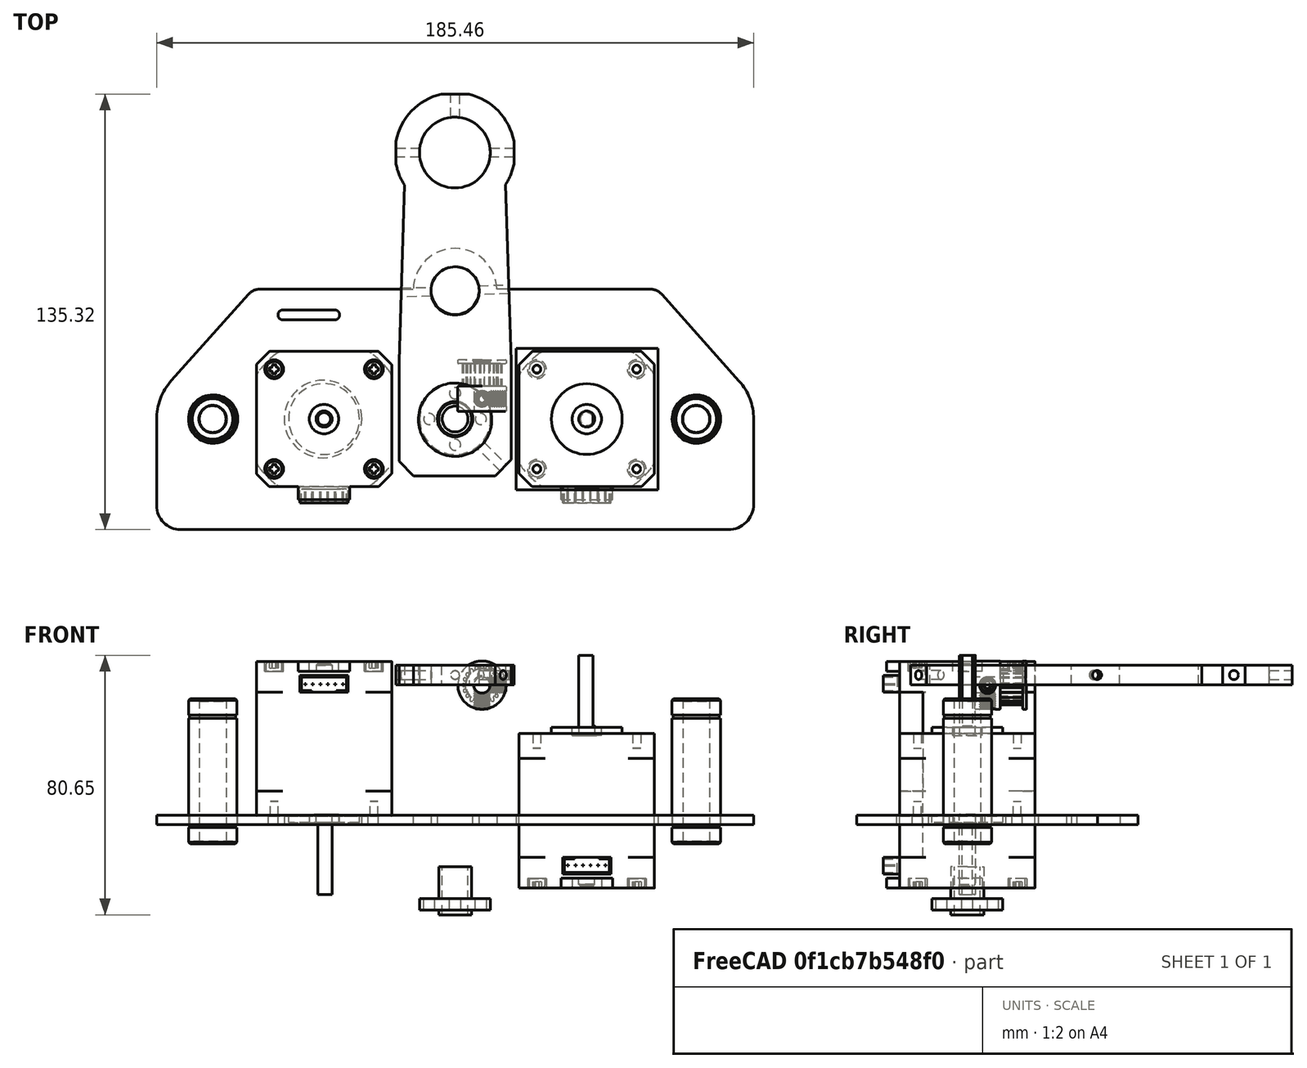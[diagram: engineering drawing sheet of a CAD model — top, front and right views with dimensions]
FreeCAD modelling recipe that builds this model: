
FCSTD DOCUMENT  (FreeCAD 1.0R38641 +468 (Git))
Label: ZAXIS-ASSY
License: All rights reserved
LicenseURL: https://en.wikipedia.org/wiki/All_rights_reserved
objects: Part::Feature×8, Sketcher::SketchObject×6, PartDesign::Pocket×4, PartDesign::Body×4, Mesh::Feature×2, App::Part×2, PartDesign::Pad×2, PartDesign::FeatureBase×2
note: 46 computed .brp shape members not serialized (recipe doc carries the construction recipe); baked Part::Feature solids carry a one-line shape summary decoded from their .brp

FEATURE [Mesh::Feature] Arm_Base_ZHub_Top_1_0_0  label="Arm_Base_ZHub_Top_1.0.0"
  Placement = pos=(-7.1,-2.4,28.8) rot=(0,0,1;3.14159rad)
FEATURE [Mesh::Feature] Arm_Base_MotorPlate_1_1_2  label="Arm_Base_MotorPlate_1.1.2"
  Placement = pos=(0,2.2,0) rot=(0,0,1;0rad)
FEATURE [App::Part] Part  label="ZAXIS"
  Group = -> [Arm_Base_ZHub_Top_1_0_0,Arm_Base_MotorPlate_1_1_2]
  Origin = -> Origin
FEATURE [Sketcher::SketchObject] Sketch002
  ArcFitTolerance = 1e-06
  AttachmentSupport = -> [XY_Plane003]
  FullyConstrained = false
  MakeInternals = false
  MapMode = 5
  sketch-geometry (22):
    g0: Circle CenterX=0 CenterY=0 CenterZ=0 NormalX=0 NormalY=0 NormalZ=1 AngleXU=0 Radius=7.5
    g1: LineSegment [constr] StartX=-29.959 StartY=-40 StartZ=0 EndX=43.5596 EndY=-40 EndZ=0
    g2: LineSegment [constr] StartX=-51.7591 StartY=43 StartZ=0 EndX=60.4533 EndY=43 EndZ=0
    g3: Circle CenterX=0 CenterY=-40 CenterZ=0 NormalX=0 NormalY=0 NormalZ=1 AngleXU=0 Radius=11.4
    g4: Circle CenterX=0.0652184 CenterY=43 CenterZ=0 NormalX=0 NormalY=0 NormalZ=1 AngleXU=0 Radius=11
    g5: LineSegment StartX=17.4186 StartY=-21.7716 StartZ=0 EndX=15.72 EndY=32.896 EndZ=0
    g6: LineSegment StartX=-17.4186 StartY=-21.7716 StartZ=0 EndX=-15.72 EndY=33.0441 EndZ=0
    g7: LineSegment StartX=-4.33292 StartY=61.137 StartZ=0 EndX=4.33292 EndY=61.137 EndZ=0
    g8: LineSegment StartX=-18.2601 StartY=39.4677 StartZ=0 EndX=-18.2601 EndY=46.5323 EndZ=0
    g9: LineSegment StartX=18.3596 StartY=39.4677 StartZ=0 EndX=18.3596 EndY=46.5323 EndZ=0
    g10: ArcOfCircle CenterX=0.0652184 CenterY=43 CenterZ=0 NormalX=0 NormalY=0 NormalZ=1 AngleXU=0 Radius=18.6626 StartAngle=1.8087 EndAngle=2.95117
    g11: ArcOfCircle CenterX=0.0652184 CenterY=43 CenterZ=0 NormalX=0 NormalY=0 NormalZ=1 AngleXU=0 Radius=18.6323 StartAngle=0.190736 EndAngle=1.3397
    g12: ArcOfCircle CenterX=0.0652184 CenterY=43 CenterZ=0 NormalX=0 NormalY=0 NormalZ=1 AngleXU=0 Radius=18.6323 StartAngle=5.71003 EndAngle=6.09245
    g13: ArcOfCircle CenterX=0.0652184 CenterY=43 CenterZ=0 NormalX=0 NormalY=0 NormalZ=1 AngleXU=0 Radius=18.6626 StartAngle=3.33202 EndAngle=3.70429
    g14: LineSegment [constr] StartX=0 StartY=-40 StartZ=0 EndX=-21.718 EndY=-61.718 EndZ=0
    g15: LineSegment [constr] StartX=0 StartY=-40 StartZ=0 EndX=21.718 EndY=-61.718 EndZ=0
    g16: ArcOfCircle [constr] CenterX=0 CenterY=-40 CenterZ=0 NormalX=0 NormalY=0 NormalZ=1 AngleXU=0 Radius=30.7139 StartAngle=3.92699 EndAngle=5.49779
    g17: LineSegment StartX=-17.4186 StartY=-52.4548 StartZ=0 EndX=-12.4548 EndY=-57.4186 EndZ=0
    g18: LineSegment StartX=17.4186 StartY=-52.8964 StartZ=0 EndX=12.8964 EndY=-57.4186 EndZ=0
    g19: LineSegment StartX=-12.4548 StartY=-57.4186 StartZ=0 EndX=12.8964 EndY=-57.4186 EndZ=0
    g20: LineSegment StartX=17.4186 StartY=-52.8964 StartZ=0 EndX=17.4186 EndY=-21.7716 EndZ=0
    g21: LineSegment StartX=-17.4186 StartY=-52.4548 StartZ=0 EndX=-17.4186 EndY=-21.7716 EndZ=0
  constraints (46):
    c: Coincident(g0,g-1)
    c: Diameter(g0) = 15
    c: Horizontal(g1)
    c: Horizontal(g2)
    c: PointOnObject(g3,g1)
    c: Diameter(g3) = 22.8
    c: DistanceY(g1,g0) = 40
    c: DistanceY(g0,g2) = 43
    c: PointOnObject(g4,g2)
    c: Vertical(g9)
    c: Symmetric(g8,g8,g2)
    c: Equal(g9,g8)
    c: Coincident(g10,g4)
    c: Coincident(g10,g7)
    c: Coincident(g10,g8)
    c: Coincident(g11,g4)
    c: Coincident(g11,g7)
    c: Coincident(g11,g9)
    c: Coincident(g12,g4)
    c: Coincident(g12,g9)
    c: Coincident(g12,g5)
    c: Coincident(g13,g4)
    c: Coincident(g13,g8)
    c: Coincident(g13,g6)
    c: Diameter(g4) = 22
    c: Horizontal(g9,g8)
    c: PointOnObject(g3,g-2)
    c: Symmetric(g6,g5,g-2)
    c: Coincident(g14,g3)
    c: Coincident(g15,g3)
    c: Perpendicular(g15,g14)
    c: Angle(g15,g1) = 0.785398
    c: Coincident(g16,g3)
    c: Coincident(g16,g14)
    c: Coincident(g16,g15)
    c: Symmetric(g17,g17,g14)
    c: Symmetric(g18,g18,g15)
    c: Coincident(g19,g17)
    c: Coincident(g19,g18)
    c: Horizontal(g19)
    c: Symmetric(g7,g7,g-2)
    c: Coincident(g20,g18)
    c: Coincident(g21,g17)
    c: Coincident(g21,g6)
    c: Coincident(g20,g5)
    c: Parallel(g20,g21)
FEATURE [PartDesign::Pad] Pad002
  Direction = (0,0,1)
  Length = 6
  Length2 = 10
  Profile = -> Sketch002
  ReferenceAxis = -> Sketch002 [N_Axis]
  Refine = true
  Suppressed = false
  Type = 0
FEATURE [Sketcher::SketchObject] Sketch003
  ArcFitTolerance = 1e-06
  AttachmentSupport = -> [Pad002]
  ExternalGeometry = -> [Pad002]
  FullyConstrained = false
  MakeInternals = false
  MapMode = 5
  Placement = pos=(-34.9367,-34.9367,0) rot=(0.862856,-0.357407,-0.357407;1.71777rad)
  sketch-geometry (2):
    g0: Circle CenterX=28.2843 CenterY=3 CenterZ=0 NormalX=0 NormalY=0 NormalZ=1 AngleXU=0 Radius=1.4
    g1: LineSegment [constr] StartX=28.2843 StartY=3 StartZ=0 EndX=28.2843 EndY=10.6288 EndZ=0
  constraints (4):
    c: Diameter(g0) = 2.8
    c: DistanceY(g0,g-3) = 3
    c: Coincident(g1,g0)
    c: Symmetric(g-3,g-3,g1)
FEATURE [PartDesign::Pocket] Pocket
  BaseFeature = -> Pad002
  Direction = (0.707107,0.707107,0)
  Length = 20
  Length2 = 5
  Profile = -> Sketch003
  ReferenceAxis = -> Sketch003 [N_Axis]
  Refine = true
  Suppressed = false
  Type = 0
FEATURE [Sketcher::SketchObject] Sketch004
  ArcFitTolerance = 1e-06
  AttachmentSupport = -> [Pocket]
  FullyConstrained = true
  MakeInternals = false
  MapMode = 5
  Placement = pos=(-16.7279,0.51835,0) rot=(-0.565428,0.58322,0.58322;4.17081rad)
  sketch-geometry (1):
    g0: Circle CenterX=0 CenterY=3 CenterZ=0 NormalX=0 NormalY=0 NormalZ=1 AngleXU=0 Radius=1.4
  constraints (3):
    c: PointOnObject(g0,g-2)
    c: DistanceY(g-1,g0) = 3
    c: Diameter(g0) = 2.8
FEATURE [PartDesign::Pocket] Pocket001
  BaseFeature = -> Pocket
  Direction = (0.99952,-0.0309723,-1e-16)
  Length = 5
  Length2 = 5
  Profile = -> Sketch004
  ReferenceAxis = -> Sketch004 [N_Axis]
  Refine = true
  Suppressed = false
  Type = 1
FEATURE [Sketcher::SketchObject] Sketch005
  ArcFitTolerance = 1e-06
  AttachmentSupport = -> [Pocket001]
  ExternalGeometry = -> [Pocket001]
  FullyConstrained = false
  MakeInternals = false
  MapMode = 5
  Placement = pos=(-18.2601,0,0) rot=(0.57735,-0.57735,-0.57735;2.0944rad)
  sketch-geometry (2):
    g0: LineSegment [constr] StartX=-43 StartY=8.67581 StartZ=0 EndX=-43 EndY=3 EndZ=0
    g1: Circle CenterX=-43 CenterY=3 CenterZ=0 NormalX=0 NormalY=0 NormalZ=1 AngleXU=0 Radius=1.4
  constraints (4):
    c: Symmetric(g-3,g-3,g0)
    c: Coincident(g1,g0)
    c: Diameter(g1) = 2.8
    c: DistanceY(g0,g-3) = 3
FEATURE [PartDesign::Pocket] Pocket002
  BaseFeature = -> Pocket001
  Direction = (1,0,0)
  Length = 5
  Length2 = 5
  Profile = -> Sketch005
  ReferenceAxis = -> Sketch005 [N_Axis]
  Refine = true
  Suppressed = false
  Type = 1
FEATURE [Sketcher::SketchObject] Sketch006
  ArcFitTolerance = 1e-06
  AttachmentSupport = -> [Pocket002]
  FullyConstrained = true
  MakeInternals = false
  MapMode = 5
  Placement = pos=(0,61.137,0) rot=(0,0.707107,0.707107;3.14159rad)
  sketch-geometry (1):
    g0: Circle CenterX=0 CenterY=3 CenterZ=0 NormalX=0 NormalY=0 NormalZ=1 AngleXU=0 Radius=1.35
  constraints (3):
    c: PointOnObject(g0,g-2)
    c: DistanceY(g-1,g0) = 3
    c: Diameter(g0) = 2.7
FEATURE [PartDesign::Pocket] Pocket003
  BaseFeature = -> Pocket002
  Direction = (0,-1,2e-16)
  Length = 10
  Length2 = 5
  Profile = -> Sketch006
  ReferenceAxis = -> Sketch006 [N_Axis]
  Refine = true
  Suppressed = false
  Type = 0
FEATURE [PartDesign::Body] Body002  label="ARM SHOULDER CONNECTOR ALUMINIUM"
  AllowCompound = false
  Group = -> [Sketch002,Pad002,Sketch003,Pocket,Sketch004,Pocket001,Sketch005,Pocket002,Sketch006,Pocket003]
  Origin = -> Origin003
  Placement = pos=(0,39.8,-51) rot=(0,0,1;0rad)
  Tip = -> Pocket003
FEATURE [Sketcher::SketchObject] Sketch007
  ArcFitTolerance = 1e-06
  AttachmentSupport = -> [XY_Plane004]
  FullyConstrained = false
  MakeInternals = false
  MapMode = 5
  sketch-geometry (47):
    g0: GeomPoint [constr] X=-75 Y=0 Z=0
    g1: GeomPoint [constr] X=75 Y=0 Z=0
    g2: GeomPoint [constr] X=0 Y=40 Z=0
    g3: LineSegment [constr] StartX=37.4343 StartY=32.1773 StartZ=0 EndX=53.4665 EndY=32.1773 EndZ=0
    g4: Circle CenterX=0 CenterY=40 CenterZ=0 NormalX=0 NormalY=0 NormalZ=1 AngleXU=0 Radius=7.5
    g5: Circle CenterX=-75 CenterY=0 CenterZ=0 NormalX=0 NormalY=0 NormalZ=1 AngleXU=0 Radius=7.5
    g6: Circle CenterX=75 CenterY=0 CenterZ=0 NormalX=0 NormalY=0 NormalZ=1 AngleXU=0 Radius=7.5
    g7: LineSegment StartX=-84.8065 StartY=-34.3772 StartZ=0 EndX=85.2408 EndY=-34.3772 EndZ=0
    g8: LineSegment StartX=92.7337 StartY=-0.228876 StartZ=0 EndX=92.7337 EndY=-26.8843 EndZ=0
    g9: LineSegment StartX=-92.7337 StartY=2.3e-15 StartZ=0 EndX=-92.7337 EndY=-26.45 EndZ=0
    g10: ArcOfCircle CenterX=0 CenterY=40 CenterZ=0 NormalX=0 NormalY=0 NormalZ=1 AngleXU=0 Radius=13 StartAngle=0.030839 EndAngle=3.11075
    g11: LineSegment StartX=-60.4242 StartY=40.4008 StartZ=0 EndX=-12.9938 EndY=40.4008 EndZ=0
    g12: LineSegment [constr] StartX=56.5 StartY=-15.5 StartZ=0 EndX=56.5 EndY=15.5 EndZ=0
    g13: LineSegment [constr] StartX=56.5 StartY=15.5 StartZ=0 EndX=25.5 EndY=15.5 EndZ=0
    g14: LineSegment [constr] StartX=25.5 StartY=15.5 StartZ=0 EndX=25.5 EndY=-15.5 EndZ=0
    g15: LineSegment [constr] StartX=25.5 StartY=-15.5 StartZ=0 EndX=56.5 EndY=-15.5 EndZ=0
    g16: GeomPoint [constr] X=41 Y=0 Z=0
    g17: LineSegment StartX=-63 StartY=22 StartZ=0 EndX=-63 EndY=-22 EndZ=0
    g18: LineSegment StartX=-63 StartY=-22 StartZ=0 EndX=-19 EndY=-22 EndZ=0
    g19: LineSegment StartX=-19 StartY=-22 StartZ=0 EndX=-19 EndY=22 EndZ=0
    g20: LineSegment StartX=-19 StartY=22 StartZ=0 EndX=-63 EndY=22 EndZ=0
    g21: GeomPoint [constr] X=-41 Y=0 Z=0
    g22: LineSegment StartX=60.4254 StartY=40.4008 StartZ=0 EndX=12.9938 EndY=40.4008 EndZ=0
    g23: LineSegment StartX=88.0794 StartY=11.9777 StartZ=0 EndX=64.2429 EndY=38.6909 EndZ=0
    g24: LineSegment StartX=-88.2318 StartY=11.807 StartZ=0 EndX=-64.2436 EndY=38.6901 EndZ=0
    g25: Circle CenterX=41 CenterY=0 CenterZ=0 NormalX=0 NormalY=0 NormalZ=1 AngleXU=0 Radius=12.0573
    g26: Circle CenterX=25.5 CenterY=15.5 CenterZ=0 NormalX=0 NormalY=0 NormalZ=1 AngleXU=0 Radius=1.6
    g27: Circle CenterX=56.5 CenterY=15.5 CenterZ=0 NormalX=0 NormalY=0 NormalZ=1 AngleXU=0 Radius=1.6
    g28: Circle CenterX=56.5 CenterY=-15.5 CenterZ=0 NormalX=0 NormalY=0 NormalZ=1 AngleXU=0 Radius=1.6
    g29: Circle CenterX=25.5 CenterY=-15.5 CenterZ=0 NormalX=0 NormalY=0 NormalZ=1 AngleXU=0 Radius=1.6
    g30: ArcOfCircle CenterX=37.4343 CenterY=32.3561 CenterZ=0 NormalX=0 NormalY=0 NormalZ=1 AngleXU=0 Radius=1.55 StartAngle=1.5708 EndAngle=4.71239
    g31: ArcOfCircle CenterX=53.4665 CenterY=32.3561 CenterZ=0 NormalX=0 NormalY=0 NormalZ=1 AngleXU=0 Radius=1.55 StartAngle=4.71239 EndAngle=7.85398
    g32: LineSegment StartX=37.4343 StartY=33.9061 StartZ=0 EndX=53.4665 EndY=33.9061 EndZ=0
    g33: LineSegment StartX=37.4343 StartY=30.8061 StartZ=0 EndX=53.4665 EndY=30.8061 EndZ=0
    g34: ArcOfCircle CenterX=74.3997 CenterY=-0.228876 CenterZ=0 NormalX=0 NormalY=0 NormalZ=1 AngleXU=0 Radius=18.334 StartAngle=0 EndAngle=0.728553
    g35: GeomPoint [constr] X=92.7337 Y=6.76175 Z=0
    g36: ArcOfCircle CenterX=60.4254 CenterY=35.2845 CenterZ=0 NormalX=0 NormalY=0 NormalZ=1 AngleXU=0 Radius=5.11639 StartAngle=0.728553 EndAngle=1.5708
    g37: GeomPoint [constr] X=62.7171 Y=40.4008 Z=0
    g38: ArcOfCircle CenterX=85.2408 CenterY=-26.8843 CenterZ=0 NormalX=0 NormalY=0 NormalZ=1 AngleXU=0 Radius=7.49292 StartAngle=4.71239 EndAngle=6.28319
    g39: GeomPoint [constr] X=92.7337 Y=-34.3772 Z=0
    g40: ArcOfCircle CenterX=-84.8065 CenterY=-26.45 CenterZ=0 NormalX=0 NormalY=0 NormalZ=1 AngleXU=0 Radius=7.92721 StartAngle=3.14159 EndAngle=4.71239
    g41: GeomPoint [constr] X=-92.7337 Y=-34.3772 Z=0
    g42: ArcOfCircle CenterX=-75 CenterY=1e-16 CenterZ=0 NormalX=0 NormalY=0 NormalZ=1 AngleXU=0 Radius=17.7337 StartAngle=2.41304 EndAngle=3.14159
    g43: GeomPoint [constr] X=-92.7337 Y=6.76175 Z=0
    g44: ArcOfCircle CenterX=-60.4242 CenterY=35.282 CenterZ=0 NormalX=0 NormalY=0 NormalZ=1 AngleXU=0 Radius=5.11886 StartAngle=1.5708 EndAngle=2.41304
    g45: GeomPoint [constr] X=-62.7171 Y=40.4008 Z=0
    g46: Circle CenterX=0 CenterY=0 CenterZ=0 NormalX=0 NormalY=0 NormalZ=1 AngleXU=0 Radius=5.5
  constraints (90):
    c: PointOnObject(g0,g-1)
    c: PointOnObject(g2,g-2)
    c: Horizontal(g3)
    c: Symmetric(g0,g1,g-2)
    c: Coincident(g4,g2)
    c: Diameter(g4) = 15
    c: DistanceY(g-1,g2) = 40
    c: Coincident(g5,g0)
    c: Coincident(g6,g1)
    c: Equal(g6,g5)
    c: Diameter(g6) = 15
    c: DistanceX(g0,g1) = 150
    c: Vertical(g8)
    c: Vertical(g9)
    c: Symmetric(g39,g41,g-2)
    c: Coincident(g10,g2)
    c: Radius(g10) = 13
    c: Coincident(g10,g11)
    c: Coincident(g12,g13)
    c: Coincident(g13,g14)
    c: Coincident(g14,g15)
    c: Coincident(g15,g12)
    c: Vertical(g12)
    c: Vertical(g14)
    c: Horizontal(g13)
    c: Horizontal(g15)
    c: Symmetric(g14,g12,g16)
    c: PointOnObject(g16,g-1)
    c: Coincident(g17,g18)
    c: Coincident(g18,g19)
    c: Coincident(g19,g20)
    c: Coincident(g20,g17)
    c: Vertical(g17)
    c: Vertical(g19)
    c: Horizontal(g18)
    c: Horizontal(g20)
    c: Symmetric(g19,g17,g21)
    c: Symmetric(g16,g21,g-2)
    c: Horizontal(g22)
    c: Coincident(g22,g10)
    c: Horizontal(g10,g10)
    c: Symmetric(g45,g37,g-2)
    c: Horizontal(g43,g35)
    c: Distance(g13,g12) = 31
    c: Distance(g12,g12) = 31
    c: DistanceY(g18,g19) = 44
    c: DistanceX(g17,g19) = 44
    c: DistanceX(g21,g16) = 82
    c: Coincident(g25,g16)
    c: Coincident(g26,g13)
    c: Coincident(g27,g12)
    c: Coincident(g28,g12)
    c: Coincident(g29,g14)
    c: Equal(g26,g29)
    c: Equal(g26,g28)
    c: Equal(g26,g27)
    c: Diameter(g26) = 3.2
    c: Tangent(g30,g32) = 1.5708
    c: Tangent(g30,g33) = -1.5708
    c: Tangent(g31,g32) = 1.5708
    c: Tangent(g31,g33) = -1.5708
    c: Equal(g30,g31)
    c: Horizontal(g33)
    c: Diameter(g31) = 3.1
    c: PointOnObject(g35,g8)
    c: PointOnObject(g35,g23)
    c: Tangent(g8,g34) = 1.5708
    c: Tangent(g23,g34) = -1.5708
    c: PointOnObject(g37,g22)
    c: PointOnObject(g37,g23)
    c: Tangent(g22,g36) = -1.5708
    c: Tangent(g23,g36) = -1.5708
    c: PointOnObject(g39,g7)
    c: PointOnObject(g39,g8)
    c: Tangent(g7,g38) = -1.5708
    c: Tangent(g8,g38) = 1.5708
    c: PointOnObject(g41,g7)
    c: PointOnObject(g41,g9)
    c: Tangent(g7,g40) = -1.5708
    c: Tangent(g9,g40) = -1.5708
    c: PointOnObject(g43,g9)
    c: PointOnObject(g43,g24)
    c: Tangent(g9,g42) = -1.5708
    c: Tangent(g24,g42) = 1.5708
    c: PointOnObject(g45,g11)
    c: PointOnObject(g45,g24)
    c: Tangent(g11,g44) = 1.5708
    c: Tangent(g24,g44) = 1.5708
    c: Coincident(g46,g-1)
    c: Diameter(g46) = 11
FEATURE [Part::Feature] Part__Feature  label="NEMA17 42-40 v3"
  Placement = pos=(40.9,0,0) rot=(0,-0.707107,0.707107;3.14159rad)
  shape: bbox 42.02 x 47.1 x 72.37 mm, 266 faces (baked)
FEATURE [PartDesign::Pad] Pad003
  Direction = (0,0,1)
  Length = 3
  Length2 = 10
  Profile = -> Sketch007
  ReferenceAxis = -> Sketch007 [N_Axis]
  Refine = true
  Suppressed = false
  Type = 0
FEATURE [PartDesign::Body] Body003  label="motor plate metal 3mm"
  AllowCompound = false
  Group = -> [Sketch007,Pad003]
  Origin = -> Origin004
  Tip = -> Pad003
FEATURE [PartDesign::FeatureBase] Clone
  BaseFeature = -> Body003
  Suppressed = false
FEATURE [PartDesign::Body] Body004
  AllowCompound = false
  Group = -> [Clone]
  Origin = -> Origin005
  Placement = pos=(-1.01e-14,0,-25.3) rot=(0,1,0;3.14159rad)
  Tip = -> Clone
FEATURE [Part::Feature] Part__Feature001  label="LM8LUU Long Type Linear Bearing"
  Placement = pos=(-75.3,0,-34.2) rot=(0,1,0;4.71239rad)
  shape: bbox 15 x 15 x 45 mm, 34 faces (baked)
FEATURE [Part::Feature] Part__Feature002  label="NEMA17 42-40 v004"
  Placement = pos=(-40.7,-5.7e-15,-25.6) rot=(1,0,0;1.5708rad)
  shape: bbox 42.02 x 47.1 x 72.37 mm, 266 faces (baked)
FEATURE [Part::Feature] Part__Feature003  label="LM8LUU Long Type Linear Bearing001"
  Placement = pos=(74.9,0,-34.2) rot=(0,1,0;4.71239rad)
  shape: bbox 15 x 15 x 45 mm, 34 faces (baked)
FEATURE [Part::Feature] Part__Feature004  label="NUT T8"
  Placement = pos=(0,2.6e-15,-51.3) rot=(1,0,0;3.14159rad)
  shape: bbox 22 x 22 x 15 mm, 20 faces (baked)
FEATURE [PartDesign::FeatureBase] Clone001
  BaseFeature = -> Body002
  Placement = pos=(0,39.8,-51) rot=(0,0,1;0rad)
  Suppressed = false
FEATURE [PartDesign::Body] Body
  AllowCompound = false
  Group = -> [Clone001]
  Origin = -> Origin006
  Placement = pos=(1.3e-14,0,-29.8) rot=(0,1,0;3.14159rad)
  Tip = -> Clone001
FEATURE [Part::Feature] Part__Feature005  label="GT2 Timing Pulley"
  Placement = pos=(8.36176,2.39887,15.0634) rot=(0,0,1;0rad)
  shape: bbox 16.24 x 16 x 16.24 mm, 198 faces (baked)
FEATURE [Part::Feature] Part__Feature006  label="M4 grub Screw"
  Placement = pos=(10.7618,6.20089,15.0634) rot=(0.447214,0.447214,-0.774597;1.82348rad)
  shape: bbox 5 x 4.758 x 5.494 mm, 36 faces (baked)
FEATURE [Part::Feature] Part__Feature007  label="M4 grub Screw001"
  Placement = pos=(8.36176,6.20089,12.6634) rot=(-0.186157,0.694747,-0.694747;2.77349rad)
  shape: bbox 5.494 x 4.758 x 5 mm, 36 faces (baked)
FEATURE [App::Part] GT2_Pulley_Assembly_With_Grub_Screws  label="GT2 Pulley Assembly With Grub Screws"
  Group = -> [Part__Feature005,Part__Feature006,Part__Feature007]
  Origin = -> Origin007
  Placement = pos=(-48.9,-15,-27.3) rot=(1,0,0;4.71239rad)
